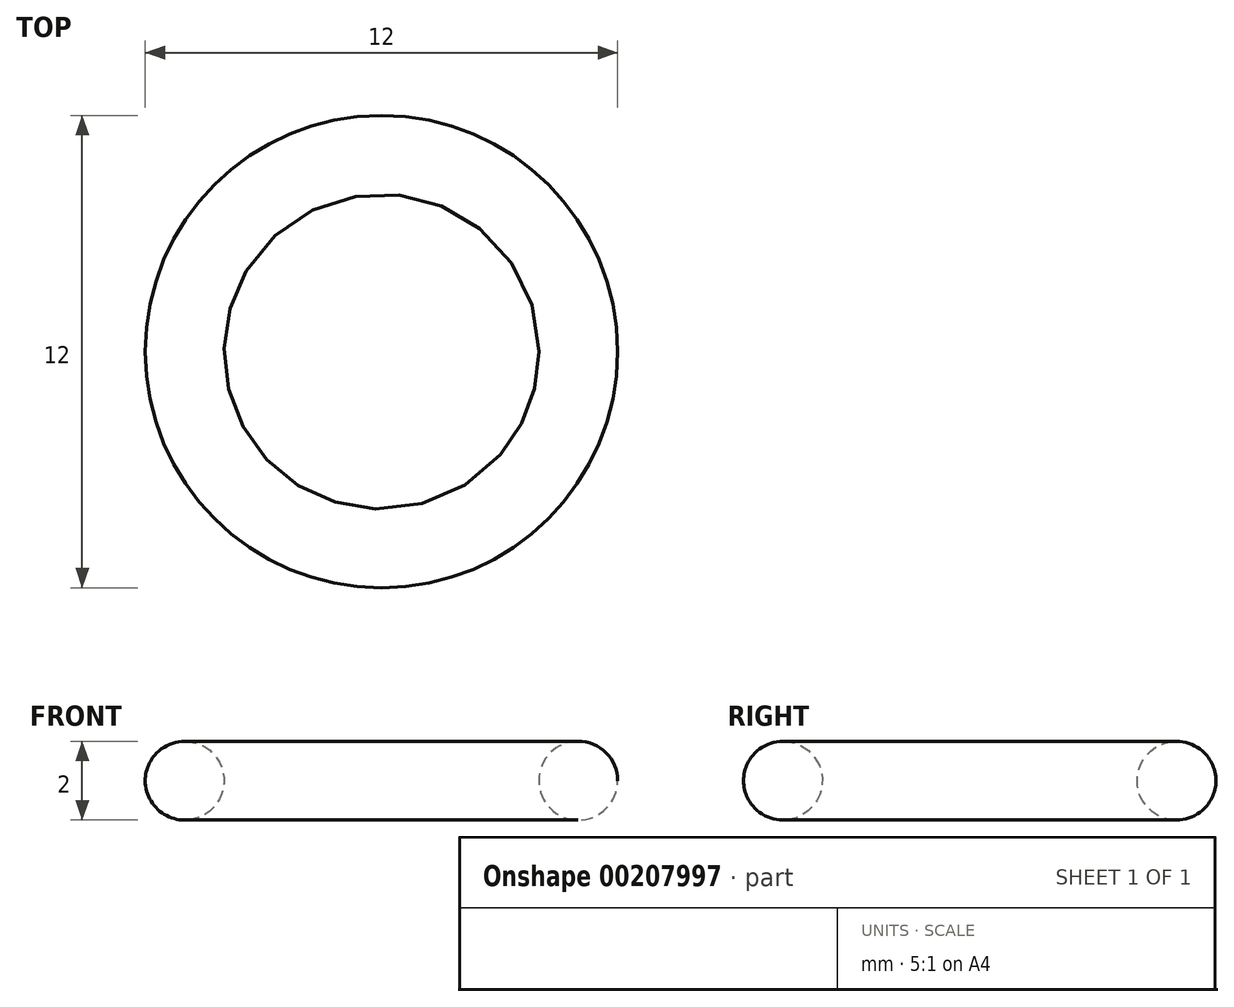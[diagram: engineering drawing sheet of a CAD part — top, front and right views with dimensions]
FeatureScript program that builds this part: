
annotation { "Feature Type Name" : "Feature", "Feature Type Description" : "" }
export const myFeature = defineFeature(function(context is Context, id is Id, definition is map)
    precondition{}
    {
        {
            var Q0;
            Q0=qCreatedBy(makeId("Front.planeOp"),FACE);
            var sketch = newSketch(context, id + "F0", { "sketchPlane" : qUnion([Q0])});
            skCircle(sketch, "E0", {"center": v(-5, 0) * mm, "radius": 1 * mm});
            skLineSegment(sketch, "E1", {"start": v(0, 2.52) * mm, "end": v(0, -3.26) * mm});
            skSolve(sketch);
        }
        {
            var Q0;
            Q0 = qSketchRegion(id + "F0", true);
            var Q1;
            Q1=sQuery(id+"F0.wireOp",EDGE,"E1");
            revolve(context, id + "F1", {"entities" : qUnion([Q0]), "axis" : qUnion([Q1]), "revolveType" : RevolveType.FULL});
        }
    });
